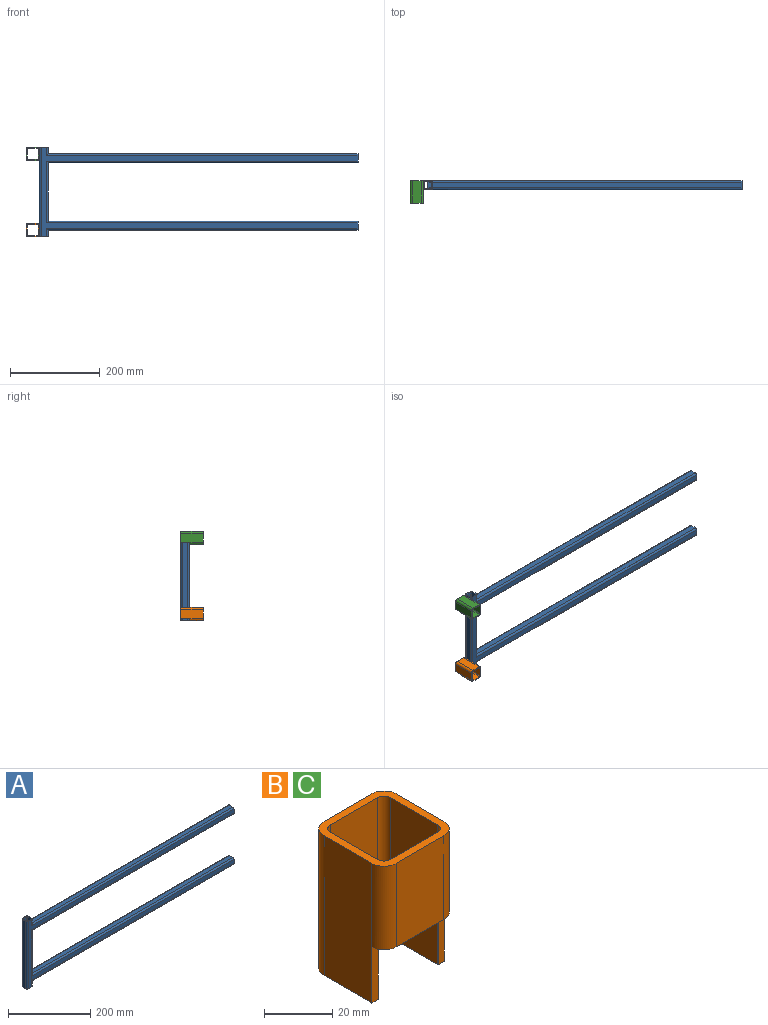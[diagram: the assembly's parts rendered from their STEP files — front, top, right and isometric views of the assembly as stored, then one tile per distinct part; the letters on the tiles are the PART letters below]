
ASSEMBLY  parts=3 mates=1
PART A: 100 faces, bbox 710x20x200 mm
  f0: plane 690x12mm, normal (0,0,-1), area 8280mm2, adj f1,f5,f14,f99
  f1: cylinder r=2mm len=690.54mm, axis (1,0,0), area 2168.3mm2, adj f0,f12,f14,f97
  f2: cylinder r=2mm len=690.54mm, axis (1,0,0), area 2168.3mm2, adj f3,f12,f14,f97
  f3: plane 690x12mm, normal (0,0,1), area 8280mm2, adj f2,f4,f14,f99
  f4: cylinder r=2mm len=690.54mm, axis (1,0,0), area 2168.3mm2, adj f3,f13,f14,f98
  f5: cylinder r=2mm len=690.54mm, axis (1,0,0), area 2168.3mm2, adj f0,f13,f14,f98
  f6: cylinder r=4mm len=694mm, axis (1,0,0), area 4344.1mm2, adj f7,f14,f15,f75
  f7: plane 690x12mm, normal (0,0,-1), area 8280mm2, adj f6,f8,f14,f74
  f8: cylinder r=4mm len=694mm, axis (1,0,0), area 4344.1mm2, adj f7,f14,f16,f77
  f9: cylinder r=4mm len=694mm, axis (1,0,0), area 4344.1mm2, adj f10,f14,f16,f54
  f10: plane 690x12mm, normal (0,0,1), area 8280mm2, adj f9,f11,f14,f55
  f11: cylinder r=4mm len=694mm, axis (1,0,0), area 4344.1mm2, adj f10,f14,f15,f56
  f12: plane 690.54x12mm, normal (0,-1,0), area 8286.4mm2, adj f1,f2,f14,f97
  f13: plane 690.54x12mm, normal (0,1,0), area 8286.4mm2, adj f4,f5,f14,f98
  f14: plane 20x20mm, normal (1,0,0), area 133.7mm2, adj f0,f1,f2,f3,f4,f5,f6,f7
  f15: plane 706x200mm, normal (0,-1,0), area 19056mm2, adj f6,f11,f14,f42,f49,f50,f51,f56
  f16: plane 706x200mm, normal (0,1,0), area 19056mm2, adj f8,f9,f14,f38,f49,f50,f53,f54
  f17: cylinder r=2mm len=16mm, axis (0,0,-1), area 45.7mm2, adj f18,f27,f32,f82
  f18: plane 16x12mm, normal (-1,0,0), area 192mm2, adj f17,f19,f23,f26
  f19: cylinder r=2mm len=16mm, axis (0,0,-1), area 45.7mm2, adj f18,f24,f25,f90
  f20: cylinder r=4mm len=16mm, axis (0,0,-1), area 31.6mm2, adj f21,f68,f69,f70
  f21: plane 16x12mm, normal (1,0,0), area 192mm2, adj f20,f22,f67,f71
  f22: cylinder r=4mm len=16mm, axis (0,0,-1), area 31.6mm2, adj f21,f64,f65,f66
  f23: plane 12x8mm, normal (0,0,-1), area 96mm2, adj f18,f24,f32,f33
  f24: cylinder r=2mm len=8mm, axis (1,0,0), area 22.8mm2, adj f19,f23,f33,f90
  f25: cylinder r=2mm len=8mm, axis (1,0,0), area 22.8mm2, adj f19,f26,f28,f90
  f26: plane 12x8mm, normal (0,0,1), area 96mm2, adj f18,f25,f27,f28
  f27: cylinder r=2mm len=8mm, axis (1,0,0), area 22.8mm2, adj f17,f26,f28,f82
  f28: plane 16x4mm, normal (-1,0,0), area 33mm2, adj f25,f26,f27,f29,f30,f31,f82,f90
  f29: cylinder r=4mm len=8mm, axis (1,0,0), area 15.8mm2, adj f28,f30,f40,f82
  f30: plane 12x8mm, normal (0,0,-1), area 96mm2, adj f28,f29,f31,f39
  f31: cylinder r=4mm len=8mm, axis (1,0,0), area 15.8mm2, adj f28,f30,f37,f90
  f32: cylinder r=2mm len=8mm, axis (1,0,0), area 22.8mm2, adj f17,f23,f33,f82
  f33: plane 16x4mm, normal (-1,0,0), area 33mm2, adj f23,f24,f32,f34,f35,f36,f82,f90
  f34: cylinder r=4mm len=8mm, axis (1,0,0), area 15.8mm2, adj f33,f35,f76,f90
  f35: plane 12x8mm, normal (0,0,1), area 96mm2, adj f33,f34,f36,f72
  f36: cylinder r=4mm len=8mm, axis (1,0,0), area 15.8mm2, adj f33,f35,f73,f82
  f37: cylinder r=2mm len=15.54mm, axis (0,0,-1), area 47.9mm2, adj f31,f39,f50,f90
  f38: cylinder r=4mm len=19mm, axis (0,0,-1), area 103.4mm2, adj f16,f41,f50,f60
  f39: plane 15x12mm, normal (-1,0,0), area 180mm2, adj f30,f37,f40,f50
  f40: cylinder r=2mm len=15.54mm, axis (0,0,-1), area 47.9mm2, adj f29,f39,f50,f82
  f41: plane 15x12mm, normal (1,0,0), area 180mm2, adj f38,f42,f50,f61
  f42: cylinder r=4mm len=19mm, axis (0,0,-1), area 103.4mm2, adj f15,f41,f50,f62
  f43: plane 15x12mm, normal (-1,0,0), area 180mm2, adj f44,f48,f49,f79
  f44: cylinder r=2mm len=15.54mm, axis (0,0,-1), area 47.9mm2, adj f43,f49,f80,f90
  f45: cylinder r=2mm len=200mm, axis (0,0,-1), area 628.3mm2, adj f46,f49,f50,f90
  f46: plane 200x12mm, normal (1,0,0), area 2400mm2, adj f45,f47,f49,f50
  f47: cylinder r=2mm len=200mm, axis (0,0,-1), area 628.3mm2, adj f46,f49,f50,f82
  f48: cylinder r=2mm len=15.54mm, axis (0,0,-1), area 47.9mm2, adj f43,f49,f78,f82
  f49: plane 20x20mm, normal (0,0,1), area 133.7mm2, adj f15,f16,f43,f44,f45,f46,f47,f48
  f50: plane 20x20mm, normal (0,0,-1), area 133.7mm2, adj f15,f16,f37,f38,f39,f40,f41,f42
  f51: cylinder r=4mm len=200mm, axis (0,0,-1), area 1256.5mm2, adj f15,f49,f50,f52
  f52: plane 200x12mm, normal (-1,0,0), area 2400mm2, adj f49,f50,f51,f53
  f53: cylinder r=4mm len=200mm, axis (0,0,-1), area 1256.5mm2, adj f16,f49,f50,f52
  f54: cylinder r=4mm len=19mm, axis (0,0,-1), area 103.4mm2, adj f9,f16,f49,f55
  f55: plane 15x12mm, normal (1,0,0), area 180mm2, adj f10,f49,f54,f56
  f56: cylinder r=4mm len=19mm, axis (0,0,-1), area 103.4mm2, adj f11,f15,f49,f55
  f57: cylinder r=4mm len=694mm, axis (1,0,0), area 4344.1mm2, adj f15,f58,f63,f75
  f58: plane 690x12mm, normal (0,0,1), area 8280mm2, adj f57,f59,f63,f74
  f59: cylinder r=4mm len=694mm, axis (1,0,0), area 4344.1mm2, adj f16,f58,f63,f77
  f60: cylinder r=4mm len=694mm, axis (1,0,0), area 4344.1mm2, adj f16,f38,f61,f63
  f61: plane 690x12mm, normal (0,0,-1), area 8280mm2, adj f41,f60,f62,f63
  f62: cylinder r=4mm len=694mm, axis (1,0,0), area 4344.1mm2, adj f15,f42,f61,f63
  f63: plane 20x20mm, normal (1,0,0), area 133.7mm2, adj f15,f16,f57,f58,f59,f60,f61,f62
  f64: cylinder r=2mm len=690.54mm, axis (1,0,0), area 2168.3mm2, adj f22,f63,f65,f71
  f65: plane 690.54x12mm, normal (0,1,0), area 8286.4mm2, adj f22,f63,f64,f66
  f66: cylinder r=2mm len=690.54mm, axis (1,0,0), area 2168.3mm2, adj f22,f63,f65,f67
  f67: plane 690x12mm, normal (0,0,1), area 8280mm2, adj f21,f63,f66,f68
  f68: cylinder r=2mm len=690.54mm, axis (1,0,0), area 2168.3mm2, adj f20,f63,f67,f69
  f69: plane 690.54x12mm, normal (0,-1,0), area 8286.4mm2, adj f20,f63,f68,f70
  f70: cylinder r=2mm len=690.54mm, axis (1,0,0), area 2168.3mm2, adj f20,f63,f69,f71
  f71: plane 690x12mm, normal (0,0,-1), area 8280mm2, adj f21,f63,f64,f70
  f72: plane 130x12mm, normal (-1,0,0), area 1560mm2, adj f35,f73,f76,f85
  f73: cylinder r=2mm len=131.07mm, axis (0,0,-1), area 410mm2, adj f36,f72,f82,f86
  f74: plane 130x12mm, normal (1,0,0), area 1560mm2, adj f7,f58,f75,f77
  f75: cylinder r=4mm len=138mm, axis (0,0,-1), area 835mm2, adj f6,f15,f57,f74
  f76: cylinder r=2mm len=131.07mm, axis (0,0,-1), area 410mm2, adj f34,f72,f84,f90
  f77: cylinder r=4mm len=138mm, axis (0,0,-1), area 835mm2, adj f8,f16,f59,f74
  f78: cylinder r=4mm len=8mm, axis (1,0,0), area 15.8mm2, adj f48,f79,f81,f82
  f79: plane 12x8mm, normal (0,0,1), area 96mm2, adj f43,f78,f80,f81
  f80: cylinder r=4mm len=8mm, axis (1,0,0), area 15.8mm2, adj f44,f79,f81,f90
  f81: plane 16x4mm, normal (-1,0,0), area 33mm2, adj f78,f79,f80,f82,f83,f90,f92,f93
  f82: plane 200x12mm, normal (0,1,0), area 2316.9mm2, adj f17,f27,f28,f29,f32,f33,f36,f40
  f83: cylinder r=2mm len=8mm, axis (1,0,0), area 22.8mm2, adj f81,f82,f93,f94
  f84: cylinder r=4mm len=8mm, axis (1,0,0), area 15.8mm2, adj f76,f85,f87,f90
  f85: plane 12x8mm, normal (0,0,-1), area 96mm2, adj f72,f84,f86,f87
  f86: cylinder r=4mm len=8mm, axis (1,0,0), area 15.8mm2, adj f73,f82,f85,f87
  f87: plane 16x4mm, normal (-1,0,0), area 33mm2, adj f82,f84,f85,f86,f88,f89,f90,f91
  f88: cylinder r=2mm len=8mm, axis (1,0,0), area 22.8mm2, adj f82,f87,f89,f94
  f89: plane 12x8mm, normal (0,0,1), area 96mm2, adj f87,f88,f91,f95
  f90: plane 200x12mm, normal (0,-1,0), area 2316.9mm2, adj f19,f24,f25,f28,f31,f33,f34,f37
  f91: cylinder r=2mm len=8mm, axis (1,0,0), area 22.8mm2, adj f87,f89,f90,f96
  f92: cylinder r=2mm len=8mm, axis (1,0,0), area 22.8mm2, adj f81,f90,f93,f96
  f93: plane 12x8mm, normal (0,0,-1), area 96mm2, adj f81,f83,f92,f95
  f94: cylinder r=2mm len=16mm, axis (0,0,-1), area 45.7mm2, adj f82,f83,f88,f95
  f95: plane 16x12mm, normal (-1,0,0), area 192mm2, adj f89,f93,f94,f96
  f96: cylinder r=2mm len=16mm, axis (0,0,-1), area 45.7mm2, adj f90,f91,f92,f95
  f97: cylinder r=4mm len=16mm, axis (0,0,-1), area 31.6mm2, adj f1,f2,f12,f99
  f98: cylinder r=4mm len=16mm, axis (0,0,-1), area 31.6mm2, adj f4,f5,f13,f99
  f99: plane 16x12mm, normal (1,0,0), area 192mm2, adj f0,f3,f97,f98
PART B: 21 faces, bbox 30x30x50 mm
  f0: plane 30x25mm, normal (0,0,-1), area 185.8mm2, adj f1,f2,f3,f4,f5,f6,f7,f9
  f1: cylinder r=5.2mm len=50mm, axis (0,0,1), area 249mm2, adj f0,f10,f11,f17,f19,f20
  f2: plane 50x19.6mm, normal (1,0,0), area 980mm2, adj f0,f3,f9,f10
  f3: cylinder r=2.6mm len=50mm, axis (0,0,1), area 204.2mm2, adj f0,f2,f4,f10
  f4: plane 50x19.6mm, normal (0,-1,0), area 980mm2, adj f0,f3,f5,f10
  f5: cylinder r=2.6mm len=50mm, axis (0,0,1), area 204.2mm2, adj f0,f4,f6,f10
  f6: plane 50x19.6mm, normal (-1,0,0), area 980mm2, adj f0,f5,f7,f10
  f7: cylinder r=2.6mm len=50mm, axis (0,0,1), area 126.5mm2, adj f0,f6,f8,f10,f18,f19
  f8: plane 30x19.6mm, normal (0,1,0), area 588mm2, adj f7,f9,f10,f19
  f9: cylinder r=2.6mm len=50mm, axis (0,0,1), area 126.5mm2, adj f0,f2,f8,f10,f19,f20
  f10: plane 30x30mm, normal (0,0,1), area 267.6mm2, adj f1,f2,f3,f4,f5,f6,f7,f8
  f11: plane 30x19.6mm, normal (0,-1,0), area 588mm2, adj f1,f10,f12,f19
  f12: cylinder r=5.2mm len=50mm, axis (0,0,1), area 249mm2, adj f0,f10,f11,f13,f18,f19
  f13: plane 50x19.6mm, normal (1,0,0), area 980mm2, adj f0,f10,f12,f14
  f14: cylinder r=5.2mm len=50mm, axis (0,0,1), area 408.4mm2, adj f0,f10,f13,f15
  f15: plane 50x19.6mm, normal (0,1,0), area 980mm2, adj f0,f10,f14,f16
  f16: cylinder r=5.2mm len=50mm, axis (0,0,1), area 408.4mm2, adj f0,f10,f15,f17
  f17: plane 50x19.6mm, normal (-1,0,0), area 980mm2, adj f0,f1,f10,f16
  f18: plane 20x2.6mm, normal (0,-1,0), area 52.1mm2, adj f0,f7,f12,f19
  f19: plane 29.99x5mm, normal (0,0,-1), area 81.8mm2, adj f1,f7,f8,f9,f11,f12,f18,f20
  f20: plane 20x2.6mm, normal (0,-1,0), area 52.1mm2, adj f0,f1,f9,f19
PART C: same geometry as B
PLACE A t=(-409.83,-17.27,30.23)mm fixed
PLACE B rot(axis=(1,0,0),90deg) t=(-434.83,-7.27,-54.77)mm
PLACE C rot(axis=(1,0,0),90deg) t=(-434.83,-7.27,115.23)mm
MATE planar A.f52 <-> B.f13  axis (-1,0,0) through (-419.83,-17.27,30.23)mm
